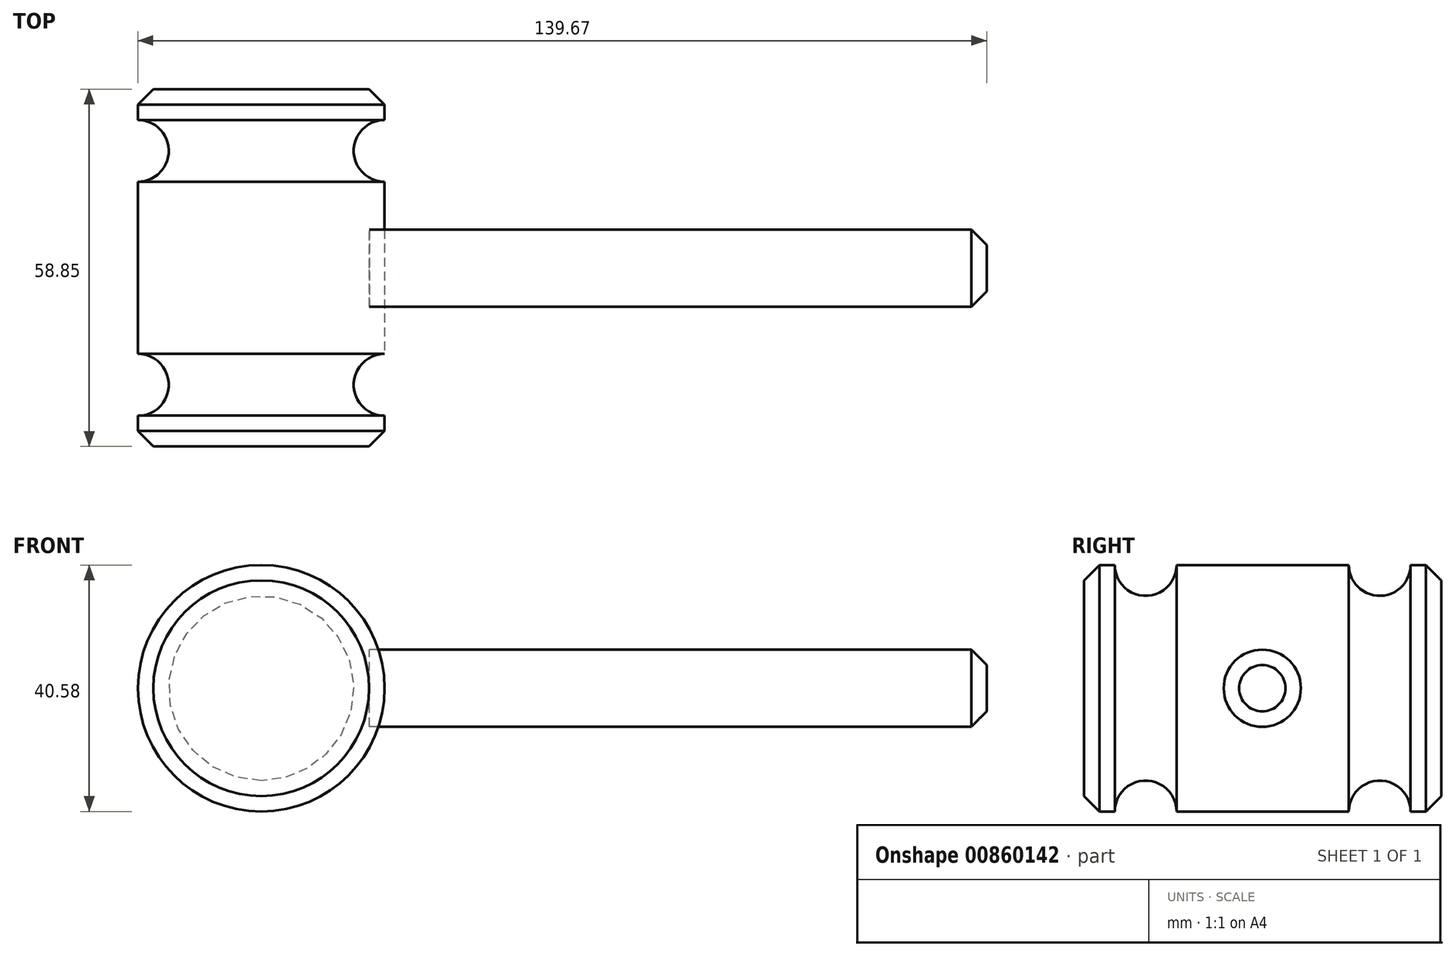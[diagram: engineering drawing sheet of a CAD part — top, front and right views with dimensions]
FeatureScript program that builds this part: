
annotation { "Feature Type Name" : "Feature", "Feature Type Description" : "" }
export const myFeature = defineFeature(function(context is Context, id is Id, definition is map)
    precondition{}
    {
        {
            var Q0;
            Q0=qCreatedBy(makeId("Top.planeOp"),FACE);
            var sketch = newSketch(context, id + "F0", { "sketchPlane" : qUnion([Q0])});
            skLineSegment(sketch, "E0.bottom", {"start": v(0, 0) * mm, "end": v(20.3, 0) * mm});
            skLineSegment(sketch, "E0.top", {"start": v(0, 58.85) * mm, "end": v(20.3, 58.85) * mm});
            skLineSegment(sketch, "E0.left", {"start": v(0, 0) * mm, "end": v(0, 58.85) * mm});
            skLineSegment(sketch, "E0.right", {"start": v(20.3, 0) * mm, "end": v(20.3, 5.08) * mm});
            skArc(sketch, "E1", {"start": v(20.3, 53.77) * mm, "mid": v(15.21, 48.69) * mm, "end": v(20.3, 43.6) * mm});
            skArc(sketch, "E2", {"start": v(20.3, 15.24) * mm, "mid": v(15.21, 10.16) * mm, "end": v(20.3, 5.08) * mm});
            skLineSegment(sketch, "E3.trimOffspring", {"start": v(20.3, 53.77) * mm, "end": v(20.3, 58.85) * mm});
            skLineSegment(sketch, "E4.trimOffspring", {"start": v(20.3, 15.24) * mm, "end": v(20.3, 43.6) * mm});
            skSolve(sketch);
        }
        {
            var Q0;
            Q0=makeQuery(id+"F0.imprint","IMPRINT",FACE,{"disambiguationData":[TD([[makeQuery(id+"F0.imprint","IMPRINT",EDGE,{"derivedFrom":sQuery(id+"F0.wireOp",EDGE,"E0.bottom")}),1.0]])]});
            var Q1;
            Q1=sQuery(id+"F0.wireOp",EDGE,"E0.left");
            revolve(context, id + "F1", {"surfaceOperationType" : NewSurfaceOperationType.NEW, "entities" : qUnion([Q0]), "axis" : qUnion([Q1]), "revolveType" : RevolveType.FULL});
        }
        {
            var Q0;
            Q0=qCreatedBy(makeId("Right.planeOp"),FACE);
            cPlane(context, id + "F2", {"entities" : qUnion([Q0]), "cplaneType" : CPlaneType.OFFSET, "offset" : 17.78 * mm, "width" : 152.4 * mm, "height" : 152.4 * mm});
        }
        {
            var Q0;
            Q0=qCreatedBy(id+"F2.planeOp",FACE);
            var sketch = newSketch(context, id + "F3", { "sketchPlane" : qUnion([Q0])});
            skCircle(sketch, "E5", {"center": v(29.36, 0) * mm, "radius": 6.35 * mm});
            skSolve(sketch);
        }
        {
            var Q0;
            Q0=makeQuery(id+"F3.imprint","IMPRINT",FACE,{"disambiguationData":[TD([[makeQuery(id+"F3.imprint","IMPRINT",EDGE,{"derivedFrom":sQuery(id+"F3.wireOp",EDGE,"E5")}),1.0]])]});
            extrude(context, id + "F4", {"entities" : qUnion([Q0]), "depth" : 101.6 * mm, "offsetDistance" : 25.4 * mm});
        }
        {
            var Q0;
            Q0=makeQuery(id+"F1.opRevolve","SWEPT_FACE",FACE,{"disambiguationData":[OSD([sQuery(id+"F0.wireOp",EDGE,"E0.bottom")])]});
            var Q1;
            Q1=makeQuery(id+"F1.opRevolve","SWEPT_FACE",FACE,{"disambiguationData":[OSD([sQuery(id+"F0.wireOp",EDGE,"E0.top")])]});
            var Q2;
            Q2=makeQuery(id+"F4.opExtrude","CAP_FACE",FACE,{"disambiguationData":[OSD([sQuery(id+"F3.wireOp",EDGE,"E5")])],"isStart":false});
            chamfer(context, id + "F5", {"entities" : qUnion([Q0, Q1, Q2]), "width" : 2.54 * mm, "tangentPropagation" : true});
        }
    });
